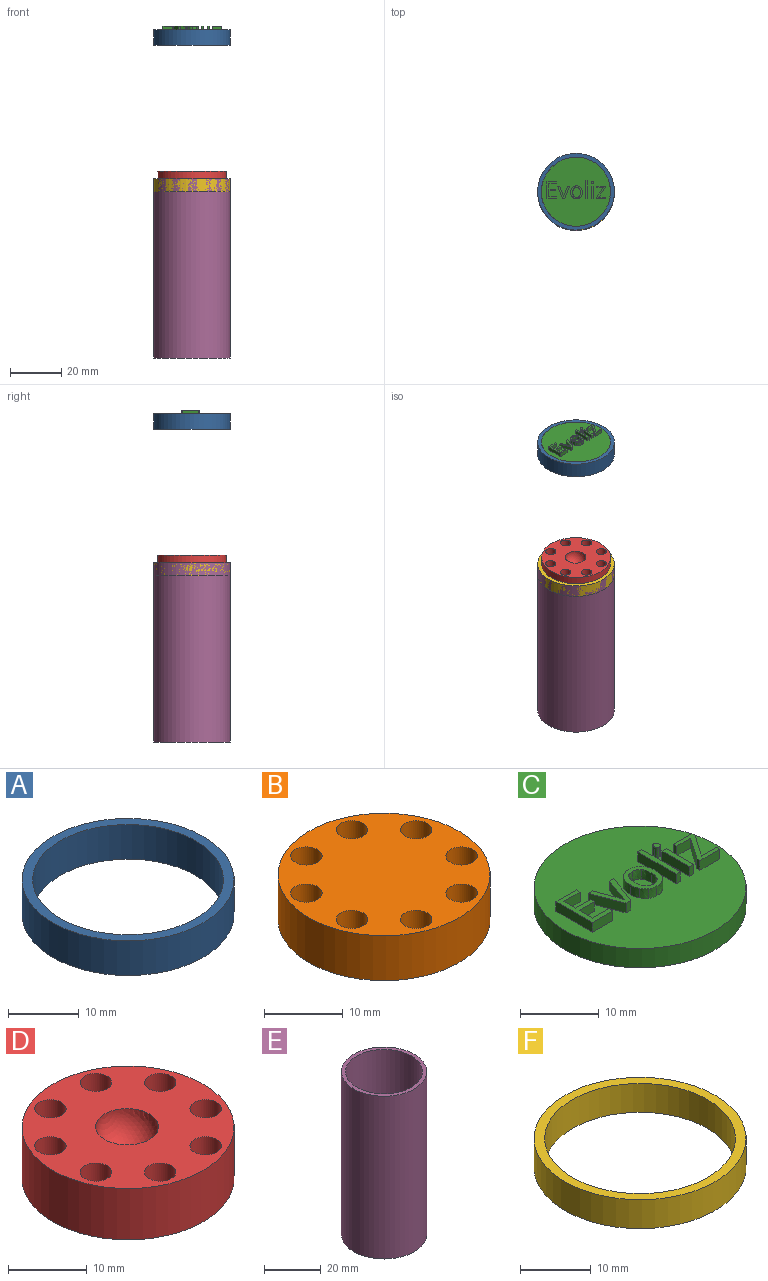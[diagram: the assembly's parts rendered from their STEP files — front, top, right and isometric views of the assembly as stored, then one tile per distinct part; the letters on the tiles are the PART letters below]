
ASSEMBLY  parts=6 mates=5
PART A: 4 faces, bbox 30x30x6 mm
  f0: cylinder r=13.5mm len=27mm, axis (0,0,1), area 508.9mm2, adj f2,f3
  f1: cylinder r=15mm len=30mm, axis (0,0,1), area 565.5mm2, adj f2,f3
  f2: plane 30x30mm, normal (0,0,-1), area 134.3mm2, adj f0,f1
  f3: plane 30x30mm, normal (0,0,1), area 134.3mm2, adj f0,f1
PART B: 11 faces, bbox 27x27x7 mm
  f0: cylinder r=13.5mm len=27mm, axis (0,0,-1), area 593.8mm2, adj f1,f2
  f1: plane 27x27mm, normal (0,0,-1), area 472mm2, adj f0,f3,f4,f5,f6,f7,f8,f9
  f2: plane 27x27mm, normal (0,0,1), area 472mm2, adj f0,f3,f4,f5,f6,f7,f8,f9
  f3: cylinder r=2mm len=7mm, axis (0,0,1), area 88mm2, adj f1,f2
  f4: cylinder r=2mm len=7mm, axis (0,0,1), area 88mm2, adj f1,f2
  f5: cylinder r=2mm len=7mm, axis (0,0,1), area 88mm2, adj f1,f2
  f6: cylinder r=2mm len=7mm, axis (0,0,1), area 88mm2, adj f1,f2
  f7: cylinder r=2mm len=7mm, axis (0,0,1), area 88mm2, adj f1,f2
  f8: cylinder r=2mm len=7mm, axis (0,0,1), area 88mm2, adj f1,f2
  f9: cylinder r=2mm len=7mm, axis (0,0,1), area 88mm2, adj f1,f2
  f10: cylinder r=2mm len=7mm, axis (0,0,1), area 88mm2, adj f1,f2
PART C: 76 faces, bbox 27x27x4.5 mm
  f0: plane 27x27mm, normal (0,0,1), area 519.4mm2, adj f1,f3,f4,f5,f6,f7,f8,f9
  f1: cylinder r=13.5mm len=27mm, axis (0,0,1), area 254.5mm2, adj f0,f2
  f2: plane 27x27mm, normal (0,0,-1), area 572.6mm2, adj f1
  f3: plane 1.5x0.68mm, normal (1,0,0), area 1mm2, adj f0,f4,f14,f15
  f4: plane 2.89x1.5mm, normal (0,1,0), area 4.3mm2, adj f0,f3,f5,f15
  f5: plane 2.41x1.5mm, normal (1,0,0), area 3.6mm2, adj f0,f4,f6,f15
  f6: plane 2.71x1.5mm, normal (0,-1,0), area 4.1mm2, adj f0,f5,f7,f15
  f7: plane 1.5x0.67mm, normal (1,0,0), area 1mm2, adj f0,f6,f8,f15
  f8: plane 2.71x1.5mm, normal (0,1,0), area 4.1mm2, adj f0,f7,f9,f15
  f9: plane 2.11x1.5mm, normal (1,0,0), area 3.2mm2, adj f0,f8,f10,f15
  f10: plane 2.89x1.5mm, normal (0,-1,0), area 4.3mm2, adj f0,f9,f11,f15
  f11: plane 1.5x0.68mm, normal (1,0,0), area 1mm2, adj f0,f10,f12,f15
  f12: plane 3.65x1.5mm, normal (0,1,0), area 5.5mm2, adj f0,f11,f13,f15
  f13: plane 6.55x1.5mm, normal (-1,0,0), area 9.8mm2, adj f0,f12,f14,f15
  f14: plane 3.65x1.5mm, normal (0,-1,0), area 5.5mm2, adj f0,f3,f13,f15
  f15: plane 6.55x3.65mm, normal (0,0,1), area 10.7mm2, adj f3,f4,f5,f6,f7,f8,f9,f10
  f16: plane 1.5x0.87mm, normal (0,-1,0), area 1.3mm2, adj f0,f17,f25,f26
  f17: plane 4.91x1.86mm, normal (0.93,-0.35,0), area 7.9mm2, adj f0,f16,f18,f26
  f18: plane 1.5x0.8mm, normal (0,1,0), area 1.2mm2, adj f0,f17,f19,f26
  f19: extruded ~3.25x1.5mm, area 5.2mm2, adj f0,f18,f20,f26
  f20: extruded ~1.5x0.98mm, area 1.5mm2, adj f0,f19,f21,f26
  f21: plane 1.5x0.04mm, normal (0,1,0), area 0.1mm2, adj f0,f20,f22,f26
  f22: extruded ~1.5x1.33mm, area 2.1mm2, adj f0,f21,f23,f26
  f23: plane 2.91x1.5mm, normal (0.94,0.34,0), area 4.6mm2, adj f0,f22,f24,f26
  f24: plane 1.5x0.8mm, normal (0,1,0), area 1.2mm2, adj f0,f23,f25,f26
  f25: plane 4.91x1.86mm, normal (-0.93,-0.35,0), area 7.9mm2, adj f0,f16,f24,f26
  f26: plane 4.91x4.59mm, normal (0,0,1), area 7.2mm2, adj f16,f17,f18,f19,f20,f21,f22,f23
  f27: extruded ~1.85x1.5mm, area 3mm2, adj f0,f28,f43,f44
  f28: extruded ~1.64x1.5mm, area 2.7mm2, adj f0,f27,f29,f44
  f29: extruded ~1.67x1.5mm, area 2.8mm2, adj f0,f28,f30,f44
  f30: extruded ~1.87x1.5mm, area 3mm2, adj f0,f29,f31,f44
  f31: extruded ~1.5x1.35mm, area 2.1mm2, adj f0,f30,f32,f44
  f32: extruded ~1.5x0.89mm, area 1.8mm2, adj f0,f31,f33,f44
  f33: extruded ~1.5x1.17mm, area 1.8mm2, adj f0,f32,f34,f44
  f34: extruded ~1.67x1.5mm, area 2.8mm2, adj f0,f33,f43,f44
  f35: extruded ~1.5x1.43mm, area 2.3mm2, adj f36,f42,f44,f45
  f36: extruded ~1.5x1.1mm, area 1.9mm2, adj f35,f37,f44,f45
  f37: extruded ~1.5x1.12mm, area 1.9mm2, adj f36,f38,f44,f45
  f38: extruded ~1.5x1.42mm, area 2.2mm2, adj f37,f39,f44,f45
  f39: extruded ~1.5x1.44mm, area 2.3mm2, adj f38,f40,f44,f45
  f40: extruded ~1.5x1.11mm, area 1.9mm2, adj f39,f41,f44,f45
  f41: extruded ~1.5x1.11mm, area 1.9mm2, adj f40,f42,f44,f45
  f42: extruded ~1.5x1.43mm, area 2.3mm2, adj f35,f41,f44,f45
  f43: extruded ~1.88x1.5mm, area 3mm2, adj f0,f27,f34,f44
  f44: plane 5.09x4.51mm, normal (0,0,1), area 9.3mm2, adj f27,f28,f29,f30,f31,f32,f33,f34
  f45: plane 3.83x2.97mm, normal (0,0,1), area 9.4mm2, adj f35,f36,f37,f38,f39,f40,f41,f42
  f46: plane 6.97x1.5mm, normal (1,0,0), area 10.5mm2, adj f0,f47,f49,f50
  f47: plane 1.5x0.74mm, normal (0,1,0), area 1.1mm2, adj f0,f46,f48,f50
  f48: plane 6.97x1.5mm, normal (-1,0,0), area 10.5mm2, adj f0,f47,f49,f50
  f49: plane 1.5x0.74mm, normal (0,-1,0), area 1.1mm2, adj f0,f46,f48,f50
  f50: plane 6.97x0.74mm, normal (0,0,1), area 5.2mm2, adj f46,f47,f48,f49
  f51: plane 4.91x1.5mm, normal (1,0,0), area 7.4mm2, adj f0,f52,f54,f55
  f52: plane 1.5x0.74mm, normal (0,1,0), area 1.1mm2, adj f0,f51,f53,f55
  f53: plane 4.91x1.5mm, normal (-1,0,0), area 7.4mm2, adj f0,f52,f54,f55
  f54: plane 1.5x0.74mm, normal (0,-1,0), area 1.1mm2, adj f0,f51,f53,f55
  f55: plane 4.91x0.74mm, normal (0,0,1), area 3.7mm2, adj f51,f52,f53,f54
  f56: extruded ~1.5x0.37mm, area 0.6mm2, adj f0,f57,f63,f64
  f57: extruded ~1.5x0.31mm, area 0.5mm2, adj f0,f56,f58,f64
  f58: extruded ~1.5x0.31mm, area 0.5mm2, adj f0,f57,f59,f64
  f59: extruded ~1.5x0.37mm, area 0.6mm2, adj f0,f58,f60,f64
  f60: extruded ~1.5x0.37mm, area 0.6mm2, adj f0,f59,f61,f64
  f61: extruded ~1.5x0.31mm, area 0.5mm2, adj f0,f60,f62,f64
  f62: extruded ~1.5x0.31mm, area 0.5mm2, adj f0,f61,f63,f64
  f63: extruded ~1.5x0.37mm, area 0.6mm2, adj f0,f56,f62,f64
  f64: plane 0.99x0.88mm, normal (0,0,1), area 0.7mm2, adj f56,f57,f58,f59,f60,f61,f62,f63
  f65: plane 1.5x0.58mm, normal (1,0,0), area 0.9mm2, adj f0,f66,f74,f75
  f66: plane 2.71x1.5mm, normal (0,1,0), area 4.1mm2, adj f0,f65,f67,f75
  f67: plane 3.75x2.64mm, normal (0.82,-0.58,0), area 6.9mm2, adj f0,f66,f68,f75
  f68: plane 1.5x0.58mm, normal (1,0,0), area 0.9mm2, adj f0,f67,f69,f75
  f69: plane 3.33x1.5mm, normal (0,1,0), area 5mm2, adj f0,f68,f70,f75
  f70: plane 1.5x0.58mm, normal (-1,0,0), area 0.9mm2, adj f0,f69,f71,f75
  f71: plane 2.51x1.5mm, normal (0,-1,0), area 3.8mm2, adj f0,f70,f72,f75
  f72: plane 3.82x2.68mm, normal (-0.82,0.57,0), area 7mm2, adj f0,f71,f73,f75
  f73: plane 1.5x0.51mm, normal (-1,0,0), area 0.8mm2, adj f0,f72,f74,f75
  f74: plane 3.56x1.5mm, normal (0,-1,0), area 5.3mm2, adj f0,f65,f73,f75
  f75: plane 4.91x3.56mm, normal (0,0,1), area 7mm2, adj f65,f66,f67,f68,f69,f70,f71,f72
PART D: 12 faces, bbox 27x27x8 mm
  f0: cylinder r=13.5mm len=27mm, axis (0,0,-1), area 678.6mm2, adj f1,f10
  f1: plane 27x27mm, normal (0,0,-1), area 472mm2, adj f0,f2,f3,f4,f5,f6,f7,f8
  f2: cylinder r=2mm len=8mm, axis (0,0,1), area 100.5mm2, adj f1,f10
  f3: cylinder r=2mm len=8mm, axis (0,0,1), area 100.5mm2, adj f1,f10
  f4: cylinder r=2mm len=8mm, axis (0,0,1), area 100.5mm2, adj f1,f10
  f5: cylinder r=2mm len=8mm, axis (0,0,1), area 100.5mm2, adj f1,f10
  f6: cylinder r=2mm len=8mm, axis (0,0,1), area 100.5mm2, adj f1,f10
  f7: cylinder r=2mm len=8mm, axis (0,0,1), area 100.5mm2, adj f1,f10
  f8: cylinder r=2mm len=8mm, axis (0,0,1), area 100.5mm2, adj f1,f10
  f9: cylinder r=2mm len=8mm, axis (0,0,1), area 100.5mm2, adj f1,f10
  f10: plane 27x27mm, normal (0,0,1), area 421.8mm2, adj f0,f2,f3,f4,f5,f6,f7,f8
  f11: sphere r=4mm, area 100.5mm2, adj f10
PART E: 5 faces, bbox 30x30x70 mm
  f0: plane 27x27mm, normal (0,0,1), area 572.6mm2, adj f1
  f1: cylinder r=13.5mm len=65mm, axis (0,0,-1), area 5513.5mm2, adj f0,f3
  f2: cylinder r=15mm len=70mm, axis (0,0,-1), area 6597.3mm2, adj f3,f4
  f3: plane 30x30mm, normal (0,0,1), area 134.3mm2, adj f1,f2
  f4: plane 30x30mm, normal (0,0,-1), area 706.9mm2, adj f2
PART F: 4 faces, bbox 30x30x5 mm
  f0: cylinder r=13.5mm len=27mm, axis (0,0,-1), area 424.1mm2, adj f2,f3
  f1: cylinder r=15mm len=30mm, axis (0,0,-1), area 471.2mm2, adj f2,f3
  f2: plane 30x30mm, normal (0,0,1), area 134.3mm2, adj f0,f1
  f3: plane 30x30mm, normal (0,0,-1), area 134.3mm2, adj f0,f1
PLACE A t=(14.92,34.16,110.81)mm
PLACE B t=(14.92,34.16,40.49)mm
PLACE C t=(14.89,34.16,110.81)mm
PLACE D t=(14.92,34.16,40.49)mm
PLACE E t=(14.92,34.16,-17.51)mm
PLACE F t=(14.92,34.16,40.49)mm
MATE revolute D.f0 <-> B.f0  axis (0,0,-1) through (14.92,34.16,47.49)mm
MATE revolute F.f0 <-> E.f1  axis (0,0,1) through (14.92,34.16,52.49)mm
MATE revolute F.f0 <-> B.f0  axis (0,0,-1) through (14.92,34.16,47.49)mm
MATE revolute C.f45 <-> A.f0  axis (0,0,1) through (14.92,34.16,110.81)mm
MATE cylindrical A.f0 <-> E.f2  axis (0,0,-1) through (14.92,34.16,104.81)mm
